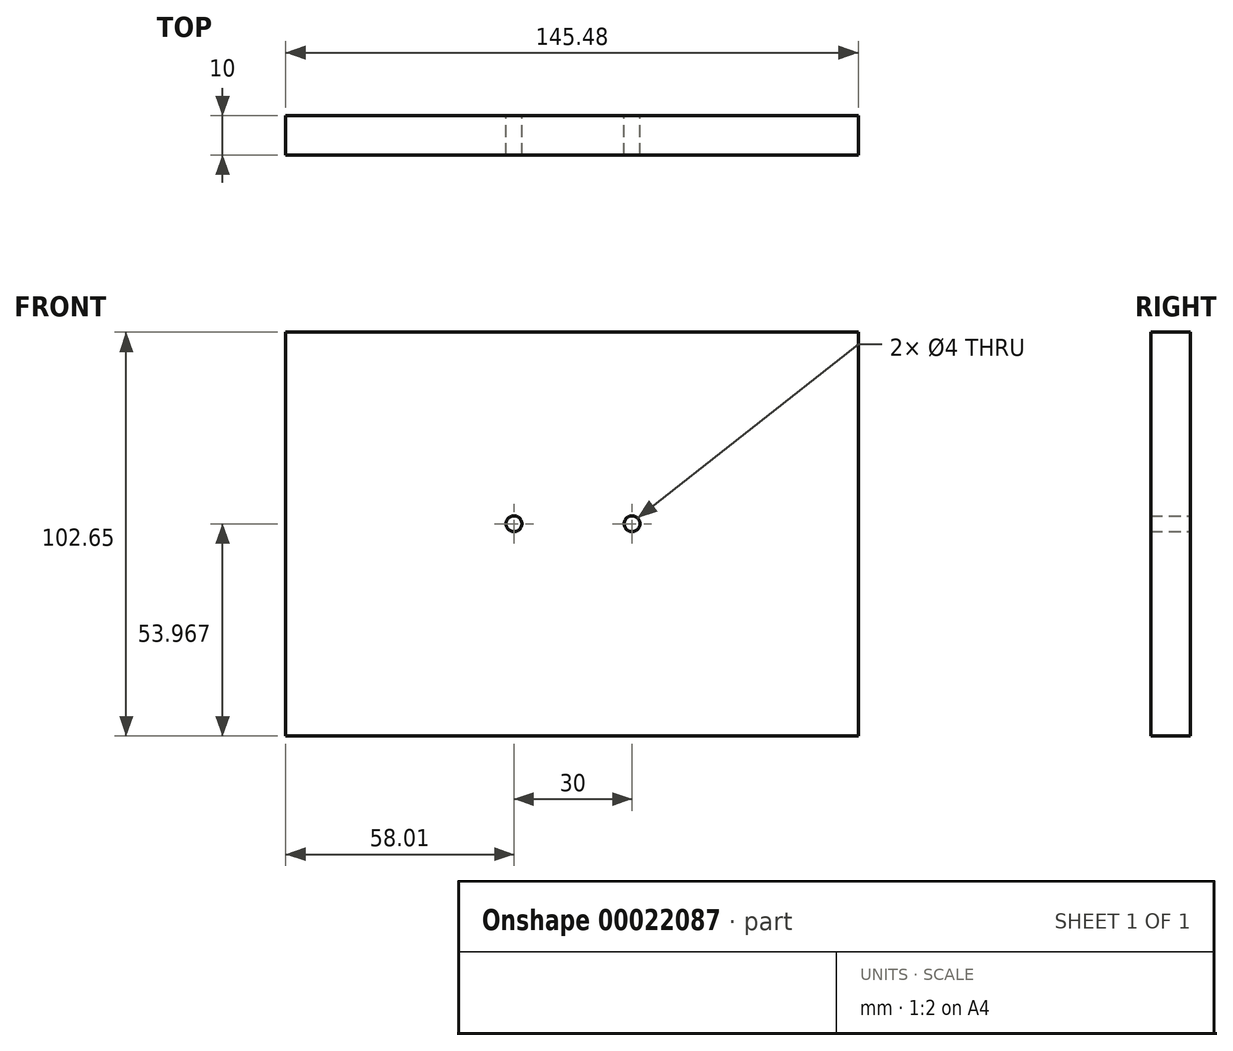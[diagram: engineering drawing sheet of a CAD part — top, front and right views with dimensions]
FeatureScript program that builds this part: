
annotation { "Feature Type Name" : "Feature", "Feature Type Description" : "" }
export const myFeature = defineFeature(function(context is Context, id is Id, definition is map)
    precondition{}
    {
        {
            var Q0;
            Q0=qCreatedBy(makeId("Front.planeOp"),FACE);
            var sketch = newSketch(context, id + "F0", { "sketchPlane" : qUnion([Q0])});
            skCircle(sketch, "E0", {"center": v(-12.36, -0.73) * mm, "radius": 2 * mm});
            skCircle(sketch, "E1", {"center": v(17.64, -0.73) * mm, "radius": 2 * mm});
            skLineSegment(sketch, "E2.bottom", {"start": v(-70.37, 47.95) * mm, "end": v(75.1, 47.95) * mm});
            skLineSegment(sketch, "E2.top", {"start": v(-70.37, -54.7) * mm, "end": v(75.1, -54.7) * mm});
            skLineSegment(sketch, "E2.left", {"start": v(-70.37, 47.95) * mm, "end": v(-70.37, -54.7) * mm});
            skLineSegment(sketch, "E2.right", {"start": v(75.1, 47.95) * mm, "end": v(75.1, -54.7) * mm});
            skSolve(sketch);
        }
        {
            var Q0;
            Q0=makeQuery(id+"F0.imprint","IMPRINT",FACE,{"disambiguationData":[TD([[makeQuery(id+"F0.imprint","IMPRINT",EDGE,{"derivedFrom":sQuery(id+"F0.wireOp",EDGE,"E0")}),-1.0]])]});
            extrude(context, id + "F1", {"entities" : qUnion([Q0]), "depth" : 10 * mm});
        }
    });
